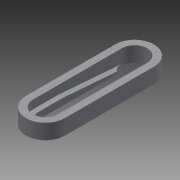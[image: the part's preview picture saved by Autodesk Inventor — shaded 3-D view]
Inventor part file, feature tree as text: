
AUTODESK INVENTOR PART (.ipt)
format: ipt  version: 2015 (Build 190159000, 159)  size: 118,784 bytes
history: native  units: mm
features: sketch x2, extrude x2, plane x1, split x1, boolean_combine x1, other x1
ambient origin geometry x8: Origin, YZ Plane, XZ Plane, XY Plane, X Axis, Y Axis, Z Axis, Center Point
bodies: Solid3 (feature_tree)
feature tree (8):
  sketch  "Sketch6"  dims[d20=3.75mm d21=2.0mm]
  extrude  "Extrusion7"  Depth=2.0mm
  sketch  "Sketch7"  dims[d22=38.0mm d23=4.5mm d24=4.5mm d25=0.0mm d28=7.5mm d29=2.0mm d30=0.5mm d31=2.0mm d32=0.0mm]
  plane  "Work Plane3"
  extrude  "Extrusion9"  Depth=4.5mm
  split  "Split1"
  boolean_combine  "Combine1"
  other  "Work Axis1"
